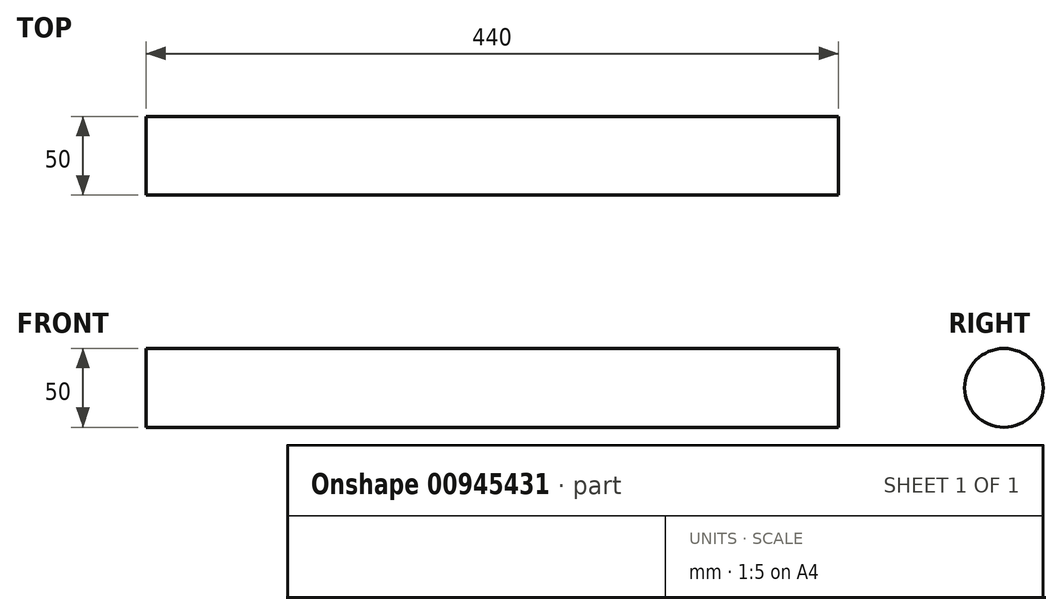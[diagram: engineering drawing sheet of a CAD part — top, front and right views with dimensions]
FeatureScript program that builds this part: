
annotation { "Feature Type Name" : "Feature", "Feature Type Description" : "" }
export const myFeature = defineFeature(function(context is Context, id is Id, definition is map)
    precondition{}
    {
        {
            var Q0;
            Q0=qCreatedBy(makeId("Right.planeOp"),FACE);
            var sketch = newSketch(context, id + "F0", { "sketchPlane" : qUnion([Q0])});
            skCircle(sketch, "E0", {"center": v(0, 0) * mm, "radius": 25 * mm});
            skSolve(sketch);
        }
        {
            var Q0;
            Q0=sQuery(id+"F0.wireOp",EDGE,"E0");
            extrude(context, id + "F1", {"bodyType" : ToolBodyType.SURFACE, "surfaceEntities" : qUnion([Q0]), "depth" : 440 * mm, "offsetDistance" : 25.4 * mm});
        }
    });
